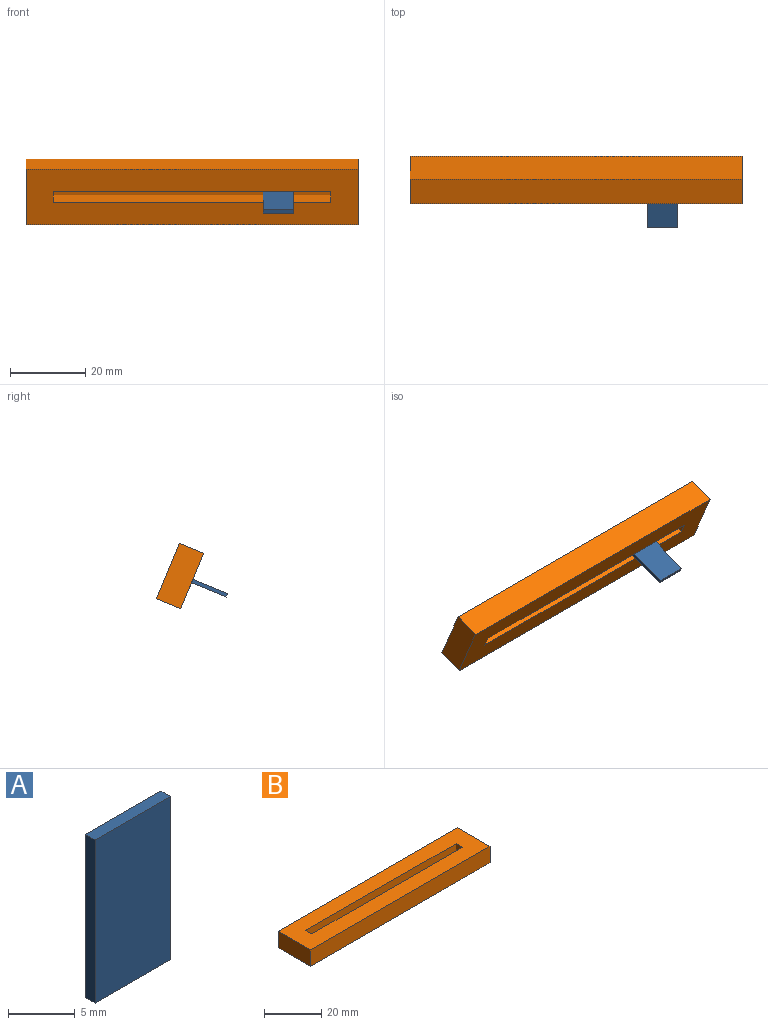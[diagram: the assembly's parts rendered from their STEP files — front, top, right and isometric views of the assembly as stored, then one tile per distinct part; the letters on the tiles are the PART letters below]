
ASSEMBLY  parts=2 mates=1
PART A: 6 faces, bbox 8x1x15 mm
  f0: plane 8x1mm, normal (0,0,1), area 8mm2, adj f1,f3,f4,f5
  f1: plane 15x1mm, normal (-1,0,0), area 15mm2, adj f0,f2,f4,f5
  f2: plane 8x1mm, normal (0,0,-1), area 8mm2, adj f1,f3,f4,f5
  f3: plane 15x1mm, normal (1,0,0), area 15mm2, adj f0,f2,f4,f5
  f4: plane 15x8mm, normal (0,-1,0), area 120mm2, adj f0,f1,f2,f3
  f5: plane 15x8mm, normal (0,1,0), area 120mm2, adj f0,f1,f2,f3
PART B: 11 faces, bbox 88.5x16x7 mm
  f0: plane 88.5x16mm, normal (0,0,1), area 1194mm2, adj f1,f2,f3,f4,f6,f7,f8,f9
  f1: plane 88.5x7mm, normal (0,1,0), area 619.5mm2, adj f0,f2,f4,f5
  f2: plane 16x7mm, normal (-1,0,0), area 112mm2, adj f0,f1,f3,f5
  f3: plane 88.5x7mm, normal (0,-1,0), area 619.5mm2, adj f0,f2,f4,f5
  f4: plane 16x7mm, normal (1,0,0), area 112mm2, adj f0,f1,f3,f5
  f5: plane 88.5x16mm, normal (0,0,-1), area 1416mm2, adj f1,f2,f3,f4
  f6: plane 74x5mm, normal (0,-1,0), area 370mm2, adj f0,f7,f9,f10
  f7: plane 5x3mm, normal (1,0,0), area 15mm2, adj f0,f6,f8,f10
  f8: plane 74x5mm, normal (0,1,0), area 370mm2, adj f0,f7,f9,f10
  f9: plane 5x3mm, normal (-1,0,0), area 15mm2, adj f0,f6,f8,f10
  f10: plane 74x3mm, normal (0,0,1), area 222mm2, adj f6,f7,f8,f9
PLACE A rot(axis=(1,0,0),112.4deg) t=(-11.88,0.14,-12.2)mm
PLACE B rot(axis=(0,-0.83,0.56),180deg) t=(-34.91,9.11,-9.03)mm
MATE slider B.f7 <-> A.f1  axis (1,0,0) through (2.09,7.84,-11.18)mm
